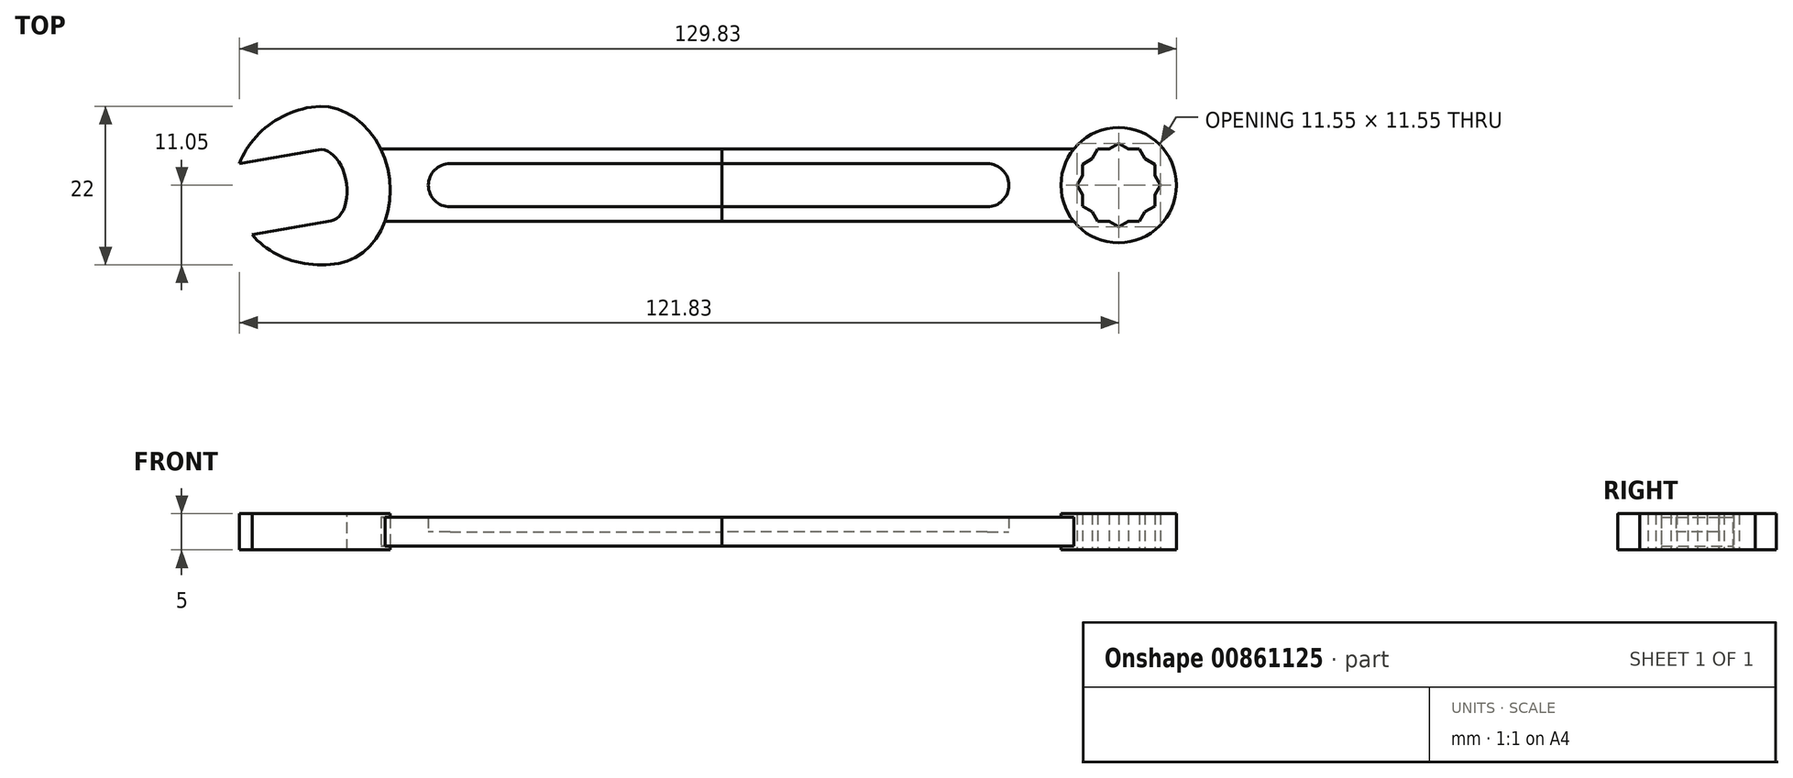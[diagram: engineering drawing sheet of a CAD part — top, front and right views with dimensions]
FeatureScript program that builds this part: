
annotation { "Feature Type Name" : "Feature", "Feature Type Description" : "" }
export const myFeature = defineFeature(function(context is Context, id is Id, definition is map)
    precondition{}
    {
        {
            var Q0;
            Q0=qCreatedBy(makeId("Top.planeOp"),FACE);
            var sketch = newSketch(context, id + "F0", { "sketchPlane" : qUnion([Q0])});
            skLineSegment(sketch, "E0", {"start": v(-55, 0) * mm, "end": v(55, 0) * mm, "construction": true});
            skLineSegment(sketch, "E1", {"start": v(-55, 0) * mm, "end": v(-56.91, 10.83) * mm, "construction": true});
            skEllipticalArc(sketch, "E2", {});
            skEllipticalArc(sketch, "E3", {});
            skEllipticalArc(sketch, "E4", {});
            skLineSegment(sketch, "E5", {"start": v(-55.87, 4.92) * mm, "end": v(-66.83, 3) * mm});
            skLineSegment(sketch, "E6", {"start": v(-54.13, -4.92) * mm, "end": v(-65.1, -6.86) * mm});
            skEllipticalArc(sketch, "E7.trimOffspring", {});
            skCircle(sketch, "E8", {"center": v(55, 0) * mm, "radius": 8 * mm});
            skCircle(sketch, "E9.cCircle", {"center": v(55, 0) * mm, "radius": 5 * mm, "construction": true});
            skLineSegment(sketch, "E9.0", {"start": v(52.11, 5) * mm, "end": v(53.66, 5) * mm});
            skLineSegment(sketch, "E9.1", {"start": v(57.89, 5) * mm, "end": v(58.66, 3.66) * mm});
            skLineSegment(sketch, "E9.2", {"start": v(60.77, 0) * mm, "end": v(60, -1.34) * mm});
            skLineSegment(sketch, "E9.3", {"start": v(57.89, -5) * mm, "end": v(56.34, -5) * mm});
            skLineSegment(sketch, "E9.4", {"start": v(52.11, -5) * mm, "end": v(51.34, -3.66) * mm});
            skLineSegment(sketch, "E9.5", {"start": v(49.23, 0) * mm, "end": v(50, 1.34) * mm});
            skPoint(sketch, "E9.0.midPoint", {"position": v(55, 5) * mm});
            skLineSegment(sketch, "E10.0", {"start": v(60, 2.89) * mm, "end": v(60, 1.34) * mm});
            skLineSegment(sketch, "E10.1", {"start": v(60, -2.89) * mm, "end": v(58.66, -3.66) * mm});
            skLineSegment(sketch, "E10.2", {"start": v(55, -5.77) * mm, "end": v(53.66, -5) * mm});
            skLineSegment(sketch, "E10.3", {"start": v(50, -2.89) * mm, "end": v(50, -1.34) * mm});
            skLineSegment(sketch, "E10.4", {"start": v(50, 2.89) * mm, "end": v(51.34, 3.66) * mm});
            skLineSegment(sketch, "E10.5", {"start": v(55, 5.77) * mm, "end": v(56.34, 5) * mm});
            skPoint(sketch, "E10.0.midPoint", {"position": v(60, 0) * mm});
            skLineSegment(sketch, "E11.trimOffspring", {"start": v(56.34, 5) * mm, "end": v(57.89, 5) * mm});
            skLineSegment(sketch, "E12.trimOffspring", {"start": v(53.66, 5) * mm, "end": v(55, 5.77) * mm});
            skLineSegment(sketch, "E13.trimOffspring", {"start": v(51.34, 3.66) * mm, "end": v(52.11, 5) * mm});
            skLineSegment(sketch, "E14.trimOffspring", {"start": v(50, 1.34) * mm, "end": v(50, 2.89) * mm});
            skLineSegment(sketch, "E15.trimOffspring", {"start": v(50, -1.34) * mm, "end": v(49.23, 0) * mm});
            skLineSegment(sketch, "E16.trimOffspring", {"start": v(51.34, -3.66) * mm, "end": v(50, -2.89) * mm});
            skLineSegment(sketch, "E17.trimOffspring", {"start": v(53.66, -5) * mm, "end": v(52.11, -5) * mm});
            skLineSegment(sketch, "E18.trimOffspring", {"start": v(56.34, -5) * mm, "end": v(55, -5.77) * mm});
            skLineSegment(sketch, "E19.trimOffspring", {"start": v(58.66, -3.66) * mm, "end": v(57.89, -5) * mm});
            skLineSegment(sketch, "E20.trimOffspring", {"start": v(60, -1.34) * mm, "end": v(60, -2.89) * mm});
            skLineSegment(sketch, "E21.trimOffspring", {"start": v(60, 1.34) * mm, "end": v(60.77, 0) * mm});
            skLineSegment(sketch, "E22.trimOffspring", {"start": v(58.66, 3.66) * mm, "end": v(60, 2.89) * mm});
            const initialGuessF0  = {"E2": [-0.055, 0, -0.17364817766693091, 0.9848077530122082, 0.005, 0.003, 3.141592653589793, 0], "E3": [-0.055, 0, -0.17364817766693, 0.9848077530122081, 0.011, 0.009, 3.141592653589793, 0], "E4": [-0.055, 0, -0.17364817766692786, 0.9848077530122086, 0.011, 0.0125, 2.0426581640745343, 3.141592653589793], "E7.trimOffspring": [-0.055, 0, -0.17364817766692786, 0.9848077530122086, 0.011, 0.0125, 6.283185307179586, 1.0989344895152575]};
            skSetInitialGuess(sketch, initialGuessF0);
            skSolve(sketch);
        }
        {
            var Q0;
            Q0=qCreatedBy(makeId("Right.planeOp"),FACE);
            var sketch = newSketch(context, id + "F1", { "sketchPlane" : qUnion([Q0])});
            skLineSegment(sketch, "E23.bottom", {"start": v(-5, 2) * mm, "end": v(5, 2) * mm});
            skLineSegment(sketch, "E23.top", {"start": v(-5, -2) * mm, "end": v(5, -2) * mm});
            skLineSegment(sketch, "E23.left", {"start": v(-5, 2) * mm, "end": v(-5, -2) * mm});
            skLineSegment(sketch, "E23.right", {"start": v(5, 2) * mm, "end": v(5, -2) * mm});
            skPoint(sketch, "E23.middle", {"position": v(0, 0) * mm});
            skSolve(sketch);
        }
        {
            var Q0;
            Q0 = qSketchRegion(id + "F0", true);
            extrude(context, id + "F2", {"entities" : qUnion([Q0]), "endBound" : BoundingType.SYMMETRIC, "depth" : 5 * mm, "offsetDistance" : 25 * mm});
        }
        {
            var Q0;
            Q0 = qSketchRegion(id + "F1", true);
            var Q1;
            Q1=makeQuery(id+"F2.opExtrude","SWEPT_FACE",FACE,{"disambiguationData":[OSD([sQuery(id+"F0.wireOp",EDGE,"E8")])]});
            var Q2;
            Q2=makeQuery(id+"F2.opExtrude","SWEPT_FACE",FACE,{"disambiguationData":[OSD([sQuery(id+"F0.wireOp",EDGE,"E8")])]});
            extrude(context, id + "F3", {"entities" : qUnion([Q0]), "operationType" : NewBodyOperationType.ADD, "endBound" : BoundingType.UP_TO_SURFACE, "depth" : 25 * mm, "endBoundEntityFace" : qUnion([Q1]), "offsetDistance" : 25 * mm});
        }
        {
            var Q0;
            Q0=makeQuery(id+"F3.opExtrude","CAP_FACE",FACE,{"disambiguationData":[OSD([sQuery(id+"F1.wireOp",EDGE,"E23.bottom"),sQuery(id+"F1.wireOp",EDGE,"E23.top"),sQuery(id+"F1.wireOp",EDGE,"E23.left"),sQuery(id+"F1.wireOp",EDGE,"E23.right")])],"isStart":true});
            var Q1;
            Q1=makeQuery(id+"F2.opExtrude","SWEPT_FACE",FACE,{"disambiguationData":[OSD([sQuery(id+"F0.wireOp",EDGE,"E3")])]});
            extrude(context, id + "F4", {"entities" : qUnion([Q0]), "endBound" : BoundingType.UP_TO_SURFACE, "depth" : 25 * mm, "endBoundEntityFace" : qUnion([Q1]), "offsetDistance" : 25 * mm});
        }
        {
            var Q0;
            Q0=qCreatedBy(makeId("Top.planeOp"),FACE);
            var sketch = newSketch(context, id + "F5", { "sketchPlane" : qUnion([Q0])});
            skArc(sketch, "E24", {"start": v(-37.66, 3) * mm, "mid": v(-40.66, 0) * mm, "end": v(-37.66, -3) * mm});
            skArc(sketch, "E25", {"start": v(36.78, -3) * mm, "mid": v(39.78, 0) * mm, "end": v(36.78, 3) * mm});
            skLineSegment(sketch, "E26", {"start": v(-37.66, 3) * mm, "end": v(36.78, 3) * mm});
            skLineSegment(sketch, "E27", {"start": v(36.78, -3) * mm, "end": v(-37.66, -3) * mm});
            skSolve(sketch);
        }
        {
            var Q0;
            Q0 = qSketchRegion(id + "F5", true);
            extrude(context, id + "F6", {"entities" : qUnion([Q0]), "operationType" : NewBodyOperationType.REMOVE, "depth" : 26.8 * mm, "offsetDistance" : 25 * mm});
        }
    });
